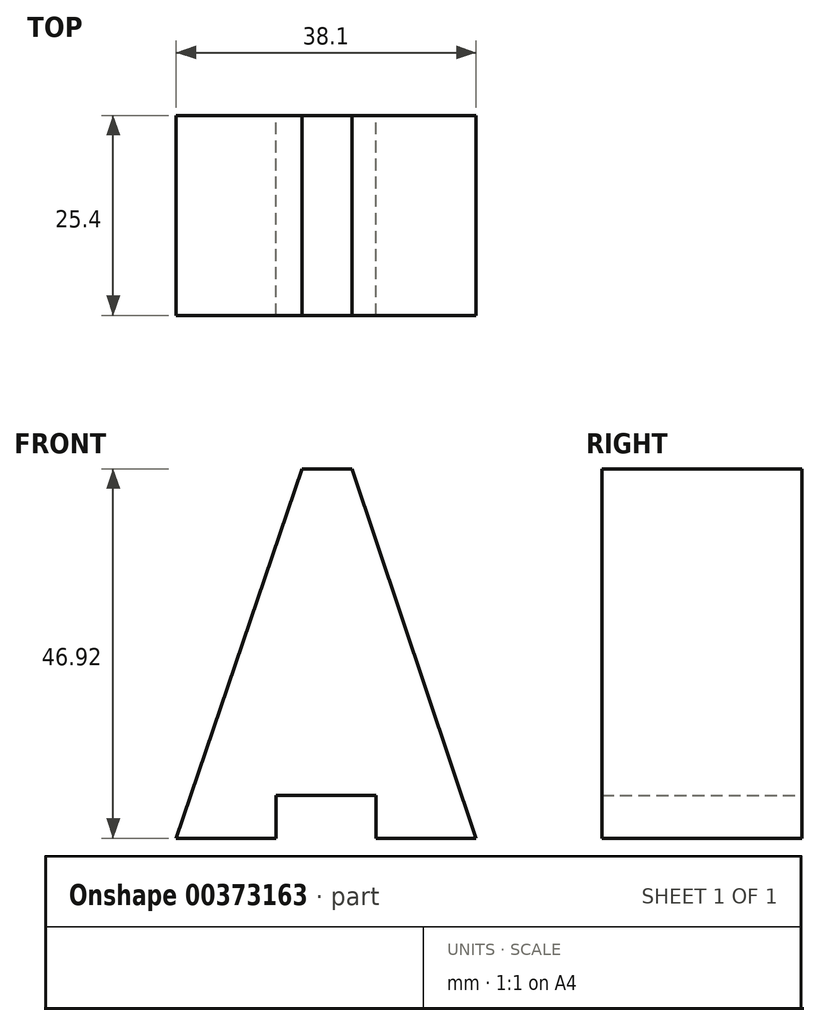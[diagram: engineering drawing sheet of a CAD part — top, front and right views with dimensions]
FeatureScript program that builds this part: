
annotation { "Feature Type Name" : "Feature", "Feature Type Description" : "" }
export const myFeature = defineFeature(function(context is Context, id is Id, definition is map)
    precondition{}
    {
        {
            var Q0;
            Q0=qCreatedBy(makeId("Front.planeOp"),FACE);
            var sketch = newSketch(context, id + "F0", { "sketchPlane" : qUnion([Q0])});
            skLineSegment(sketch, "E0", {"start": v(0, 0) * mm, "end": v(12.7, 0) * mm});
            skLineSegment(sketch, "E1", {"start": v(12.7, 0) * mm, "end": v(12.7, 5.45) * mm});
            skLineSegment(sketch, "E2", {"start": v(12.7, 5.45) * mm, "end": v(25.4, 5.45) * mm});
            skLineSegment(sketch, "E3", {"start": v(25.4, 5.45) * mm, "end": v(25.4, 0) * mm});
            skLineSegment(sketch, "E4", {"start": v(25.4, 0) * mm, "end": v(38.1, 0) * mm});
            skLineSegment(sketch, "E5", {"start": v(0, 0) * mm, "end": v(15.96, 46.92) * mm});
            skLineSegment(sketch, "E6", {"start": v(15.96, 46.92) * mm, "end": v(22.31, 46.92) * mm});
            skLineSegment(sketch, "E7", {"start": v(22.31, 46.92) * mm, "end": v(38.1, 0) * mm});
            skSolve(sketch);
        }
        {
            var Q0;
            Q0 = qSketchRegion(id + "F0", true);
            extrude(context, id + "F1", {"entities" : qUnion([Q0]), "depth" : 25.4 * mm});
        }
    });
